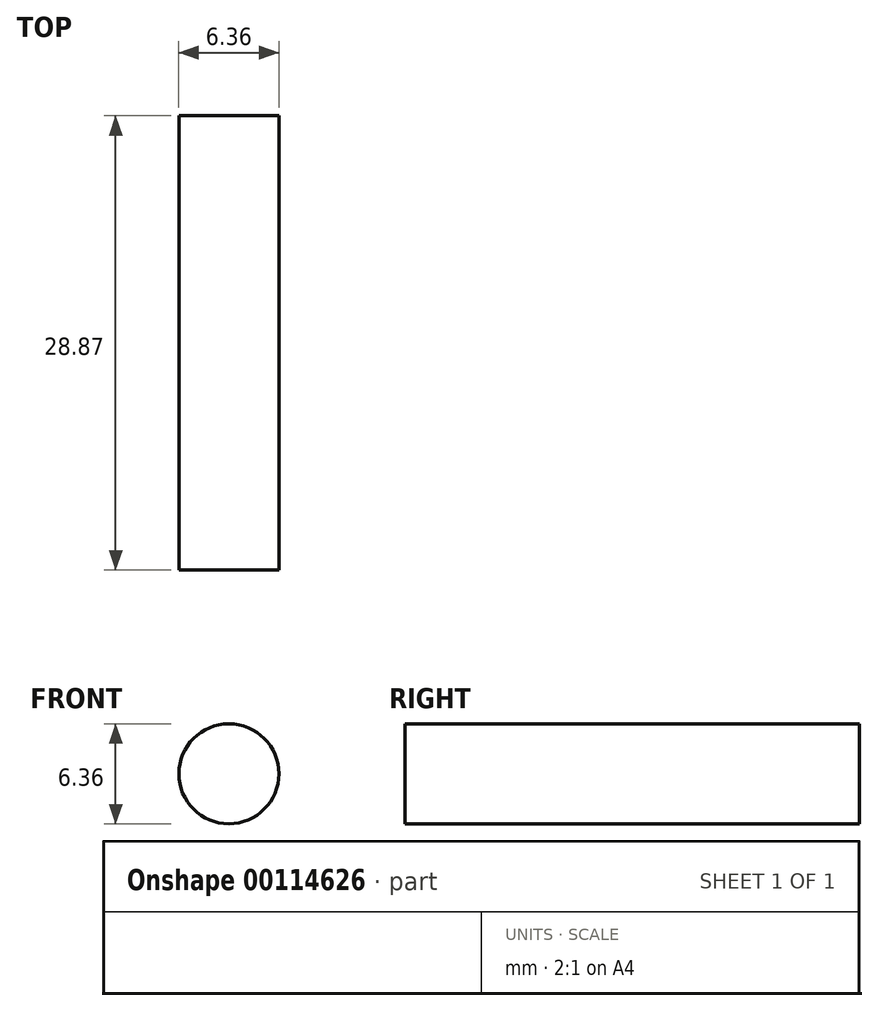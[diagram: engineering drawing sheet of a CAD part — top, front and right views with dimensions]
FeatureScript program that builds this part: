
annotation { "Feature Type Name" : "Feature", "Feature Type Description" : "" }
export const myFeature = defineFeature(function(context is Context, id is Id, definition is map)
    precondition{}
    {
        {
            var Q0;
            Q0=qCreatedBy(makeId("Front.planeOp"),FACE);
            var sketch = newSketch(context, id + "F0", { "sketchPlane" : qUnion([Q0])});
            skCircle(sketch, "E0", {"center": v(0, 0) * mm, "radius": 3.18 * mm});
            skSolve(sketch);
        }
        {
            var Q0;
            Q0 = qSketchRegion(id + "F0", true);
            extrude(context, id + "F1", {"entities" : qUnion([Q0]), "depth" : 28.87 * mm});
        }
    });
